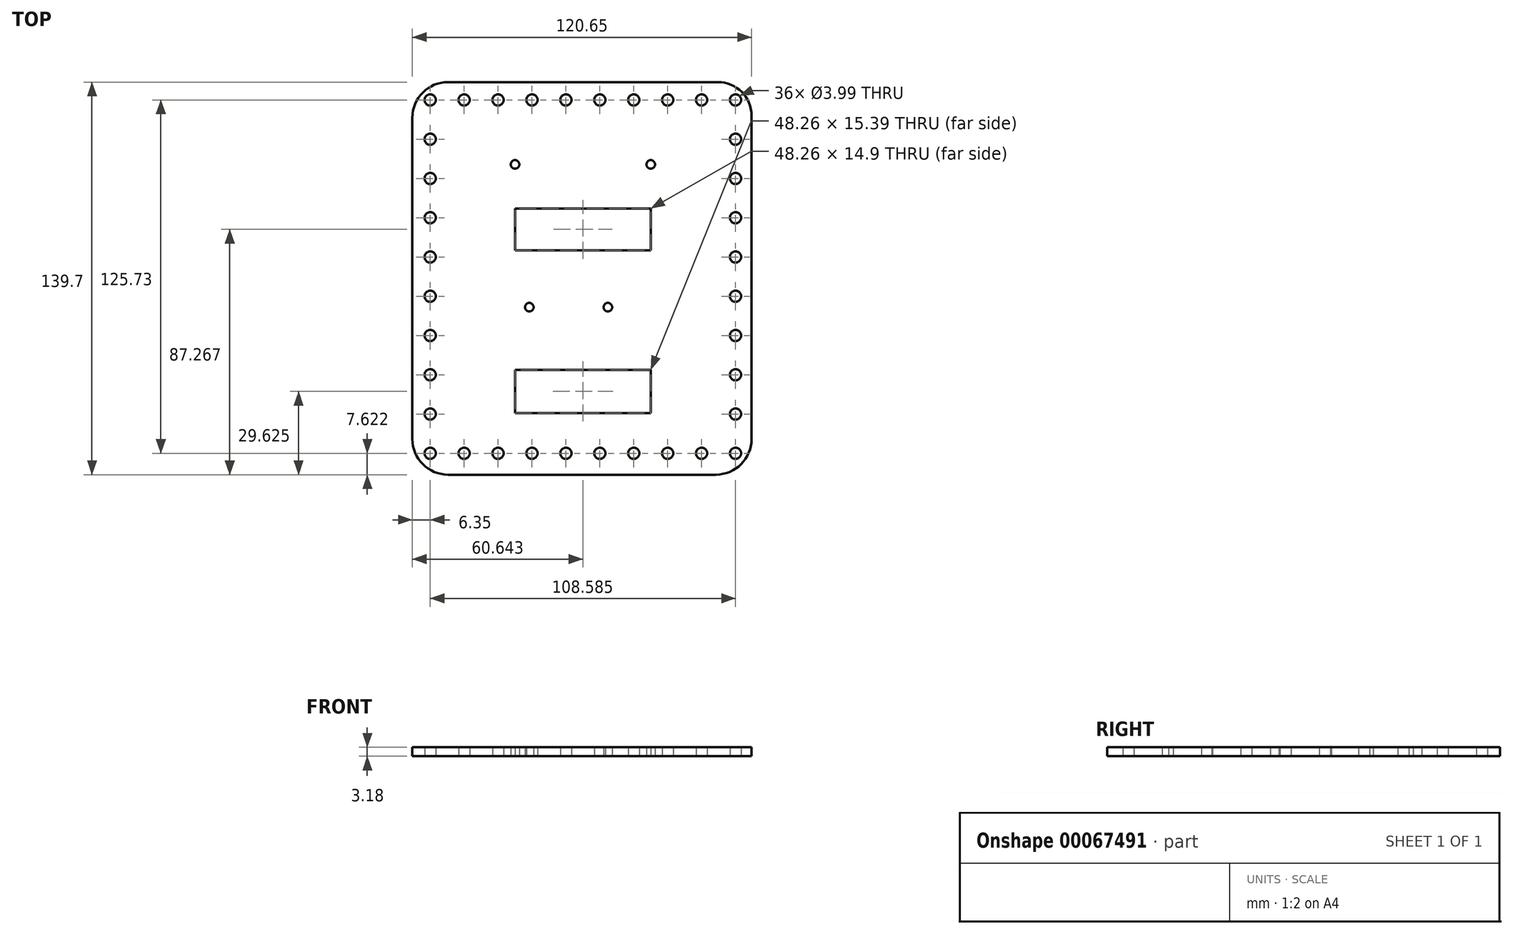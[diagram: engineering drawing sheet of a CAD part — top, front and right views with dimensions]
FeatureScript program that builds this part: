
annotation { "Feature Type Name" : "Feature", "Feature Type Description" : "" }
export const myFeature = defineFeature(function(context is Context, id is Id, definition is map)
    precondition{}
    {
        {
            var Q0;
            Q0=qCreatedBy(makeId("Top.planeOp"),FACE);
            var sketch = newSketch(context, id + "F0", { "sketchPlane" : qUnion([Q0])});
            skLineSegment(sketch, "E0.bottom", {"start": v(-491.59, 19.42) * mm, "end": v(-395.7, 19.42) * mm});
            skLineSegment(sketch, "E0.top", {"start": v(-491.59, -120.28) * mm, "end": v(-396.34, -120.28) * mm});
            skLineSegment(sketch, "E0.left", {"start": v(-504.29, 6.72) * mm, "end": v(-504.29, -107.58) * mm});
            skLineSegment(sketch, "E0.right", {"start": v(-383.64, 7.36) * mm, "end": v(-383.64, -107.58) * mm});
            skPoint(sketch, "E1.visualSharp", {"position": v(-504.29, 19.42) * mm});
            skArc(sketch, "E1.filletArc", {"start": v(-491.59, 19.42) * mm, "mid": v(-500.57, 15.7) * mm, "end": v(-504.29, 6.72) * mm});
            skPoint(sketch, "E2.visualSharp", {"position": v(-504.29, -120.28) * mm});
            skArc(sketch, "E2.filletArc", {"start": v(-504.29, -107.58) * mm, "mid": v(-500.57, -116.56) * mm, "end": v(-491.59, -120.28) * mm});
            skPoint(sketch, "E3.visualSharp", {"position": v(-383.64, -120.28) * mm});
            skArc(sketch, "E3.filletArc", {"start": v(-396.34, -120.28) * mm, "mid": v(-387.36, -116.56) * mm, "end": v(-383.64, -107.58) * mm});
            skPoint(sketch, "E4.visualSharp", {"position": v(-383.64, 19.42) * mm});
            skArc(sketch, "E4.filletArc", {"start": v(-383.64, 7.36) * mm, "mid": v(-387.17, 15.89) * mm, "end": v(-395.7, 19.42) * mm});
            skCircle(sketch, "E5", {"center": v(-497.94, 13.07) * mm, "radius": 2 * mm});
            skPoint(sketch, "E5.centerSnap0", {"position": v(-497.09, 13.07) * mm});
            skCircle(sketch, "E6.1.0.0", {"center": v(-485.87, 13.07) * mm, "radius": 2 * mm});
            skCircle(sketch, "E6.2.0.0", {"center": v(-473.8, 13.07) * mm, "radius": 2 * mm});
            skCircle(sketch, "E6.3.0.0", {"center": v(-461.74, 13.07) * mm, "radius": 2 * mm});
            skCircle(sketch, "E6.4.0.0", {"center": v(-449.68, 13.07) * mm, "radius": 2 * mm});
            skCircle(sketch, "E6.5.0.0", {"center": v(-437.61, 13.07) * mm, "radius": 2 * mm});
            skCircle(sketch, "E6.6.0.0", {"center": v(-425.55, 13.07) * mm, "radius": 2 * mm});
            skCircle(sketch, "E6.7.0.0", {"center": v(-413.48, 13.07) * mm, "radius": 2 * mm});
            skCircle(sketch, "E6.8.0.0", {"center": v(-401.42, 13.07) * mm, "radius": 2 * mm});
            skCircle(sketch, "E6.9.0.0", {"center": v(-389.35, 13.07) * mm, "radius": 2 * mm});
            skCircle(sketch, "E7.0.1.0", {"center": v(-389.35, -0.9) * mm, "radius": 2 * mm});
            skCircle(sketch, "E7.0.2.0", {"center": v(-389.35, -14.87) * mm, "radius": 2 * mm});
            skCircle(sketch, "E7.0.3.0", {"center": v(-389.35, -28.84) * mm, "radius": 2 * mm});
            skCircle(sketch, "E7.0.4.0", {"center": v(-389.35, -42.8) * mm, "radius": 2 * mm});
            skCircle(sketch, "E7.0.5.0", {"center": v(-389.35, -56.78) * mm, "radius": 2 * mm});
            skCircle(sketch, "E7.0.6.0", {"center": v(-389.35, -70.75) * mm, "radius": 2 * mm});
            skCircle(sketch, "E7.0.7.0", {"center": v(-389.35, -84.72) * mm, "radius": 2 * mm});
            skCircle(sketch, "E7.0.8.0", {"center": v(-389.35, -98.69) * mm, "radius": 2 * mm});
            skCircle(sketch, "E7.0.9.0", {"center": v(-389.35, -112.66) * mm, "radius": 2 * mm});
            skCircle(sketch, "E8.1.0.0", {"center": v(-401.42, -112.66) * mm, "radius": 2 * mm});
            skCircle(sketch, "E8.2.0.0", {"center": v(-413.48, -112.66) * mm, "radius": 2 * mm});
            skCircle(sketch, "E8.3.0.0", {"center": v(-425.55, -112.66) * mm, "radius": 2 * mm});
            skCircle(sketch, "E8.4.0.0", {"center": v(-437.61, -112.66) * mm, "radius": 2 * mm});
            skCircle(sketch, "E8.5.0.0", {"center": v(-449.68, -112.66) * mm, "radius": 2 * mm});
            skCircle(sketch, "E8.6.0.0", {"center": v(-461.74, -112.66) * mm, "radius": 2 * mm});
            skCircle(sketch, "E8.7.0.0", {"center": v(-473.8, -112.66) * mm, "radius": 2 * mm});
            skCircle(sketch, "E8.8.0.0", {"center": v(-485.87, -112.66) * mm, "radius": 2 * mm});
            skCircle(sketch, "E8.9.0.0", {"center": v(-497.94, -112.66) * mm, "radius": 2 * mm});
            skCircle(sketch, "E9.0.1.0", {"center": v(-497.94, -98.69) * mm, "radius": 2 * mm});
            skCircle(sketch, "E9.0.2.0", {"center": v(-497.94, -84.72) * mm, "radius": 2 * mm});
            skCircle(sketch, "E9.0.3.0", {"center": v(-497.94, -70.75) * mm, "radius": 2 * mm});
            skCircle(sketch, "E9.0.4.0", {"center": v(-497.94, -56.78) * mm, "radius": 2 * mm});
            skCircle(sketch, "E9.0.5.0", {"center": v(-497.94, -42.8) * mm, "radius": 2 * mm});
            skCircle(sketch, "E9.0.6.0", {"center": v(-497.94, -28.84) * mm, "radius": 2 * mm});
            skCircle(sketch, "E9.0.7.0", {"center": v(-497.94, -14.87) * mm, "radius": 2 * mm});
            skCircle(sketch, "E9.0.8.0", {"center": v(-497.94, -0.9) * mm, "radius": 2 * mm});
            skPoint(sketch, "E10.startSnap0", {"position": v(-443.65, 19.42) * mm});
            skCircle(sketch, "E11", {"center": v(-467.78, -9.88) * mm, "radius": 1.52 * mm});
            skCircle(sketch, "E12", {"center": v(-419.52, -9.88) * mm, "radius": 1.52 * mm});
            skCircle(sketch, "E13", {"center": v(-462.7, -60.68) * mm, "radius": 1.52 * mm});
            skCircle(sketch, "E14", {"center": v(-434.76, -60.68) * mm, "radius": 1.52 * mm});
            skLineSegment(sketch, "E15.bottom", {"start": v(-467.78, -25.56) * mm, "end": v(-419.52, -25.56) * mm});
            skLineSegment(sketch, "E15.top", {"start": v(-467.78, -40.47) * mm, "end": v(-419.52, -40.47) * mm});
            skLineSegment(sketch, "E15.left", {"start": v(-467.78, -25.56) * mm, "end": v(-467.78, -40.47) * mm});
            skLineSegment(sketch, "E15.right", {"start": v(-419.52, -25.56) * mm, "end": v(-419.52, -40.47) * mm});
            skLineSegment(sketch, "E16.bottom", {"start": v(-467.78, -82.96) * mm, "end": v(-419.52, -82.96) * mm});
            skLineSegment(sketch, "E16.top", {"start": v(-467.78, -98.35) * mm, "end": v(-419.52, -98.35) * mm});
            skLineSegment(sketch, "E16.left", {"start": v(-467.78, -82.96) * mm, "end": v(-467.78, -98.35) * mm});
            skLineSegment(sketch, "E16.right", {"start": v(-419.52, -82.96) * mm, "end": v(-419.52, -98.35) * mm});
            skSolve(sketch);
        }
        {
            var Q0;
            Q0=makeQuery(id+"F0.imprint","IMPRINT",FACE,{"disambiguationData":[TD([[makeQuery(id+"F0.imprint","IMPRINT",EDGE,{"derivedFrom":sQuery(id+"F0.wireOp",EDGE,"E0.bottom")}),-1.0]])]});
            extrude(context, id + "F1", {"entities" : qUnion([Q0]), "depth" : 3.17 * mm, "offsetDistance" : 25.4 * mm});
        }
    });
